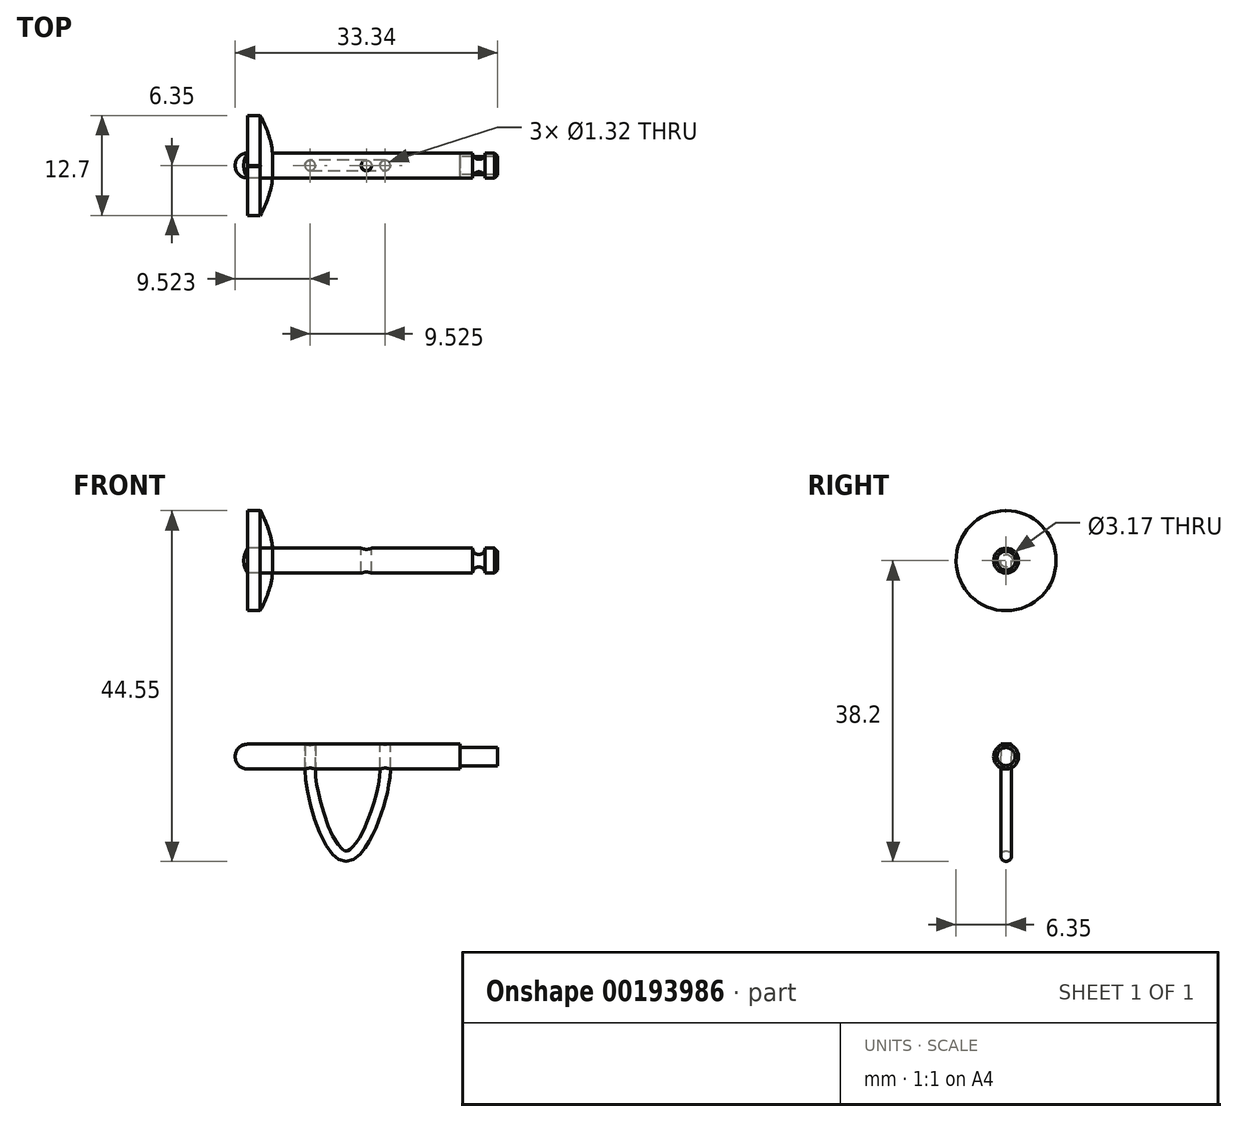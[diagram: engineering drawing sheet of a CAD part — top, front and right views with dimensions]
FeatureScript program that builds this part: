
annotation { "Feature Type Name" : "Feature", "Feature Type Description" : "" }
export const myFeature = defineFeature(function(context is Context, id is Id, definition is map)
    precondition{}
    {
        {
            var Q0;
            Q0=qCreatedBy(makeId("Front.planeOp"),FACE);
            var sketch = newSketch(context, id + "F0", { "sketchPlane" : qUnion([Q0])});
            skLineSegment(sketch, "E0", {"start": v(15.88, 0) * mm, "end": v(-15.88, 0) * mm, "construction": true});
            skLineSegment(sketch, "E1", {"start": v(-17.46, -24.9) * mm, "end": v(15.87, -24.9) * mm, "construction": true});
            skLineSegment(sketch, "E2", {"start": v(-15.88, 0) * mm, "end": v(-15.88, 1.59) * mm});
            skLineSegment(sketch, "E3", {"start": v(-15.88, 1.59) * mm, "end": v(12.7, 1.59) * mm});
            skLineSegment(sketch, "E4", {"start": v(14.29, 1.59) * mm, "end": v(15.87, 1.59) * mm});
            skLineSegment(sketch, "E5", {"start": v(15.87, 0) * mm, "end": v(15.87, 1.59) * mm});
            skLineSegment(sketch, "E6", {"start": v(-17.46, -24.9) * mm, "end": v(-17.46, -23.3) * mm});
            skLineSegment(sketch, "E7", {"start": v(-17.46, -23.3) * mm, "end": v(11.11, -23.3) * mm});
            skLineSegment(sketch, "E8", {"start": v(11.11, -23.3) * mm, "end": v(11.11, -23.75) * mm});
            skLineSegment(sketch, "E9", {"start": v(11.11, -23.75) * mm, "end": v(15.87, -23.75) * mm});
            skLineSegment(sketch, "E10", {"start": v(15.87, -23.75) * mm, "end": v(15.87, -24.9) * mm});
            skArc(sketch, "E11", {"start": v(12.7, 1.59) * mm, "mid": v(13.5, 0.8) * mm, "end": v(14.29, 1.59) * mm});
            skLineSegment(sketch, "E12", {"start": v(12.7, 1.59) * mm, "end": v(14.29, 1.59) * mm, "construction": true});
            skArc(sketch, "E13", {"start": v(-15.88, 1.59) * mm, "mid": v(-16.25, 0.83) * mm, "end": v(-16.38, 0) * mm});
            skLineSegment(sketch, "E14", {"start": v(-15.88, 0) * mm, "end": v(15.88, 0) * mm});
            skLineSegment(sketch, "E15", {"start": v(-17.46, -24.9) * mm, "end": v(15.87, -24.9) * mm});
            skLineSegment(sketch, "E16", {"start": v(-15.88, 0) * mm, "end": v(-16.38, 0) * mm, "construction": true});
            skLineSegment(sketch, "E17", {"start": v(-16.38, 0) * mm, "end": v(-16.38, 1.36) * mm, "construction": true});
            skLineSegment(sketch, "E18", {"start": v(-16.38, 0) * mm, "end": v(-15.88, 0) * mm});
            skLineSegment(sketch, "E19", {"start": v(15.87, 0) * mm, "end": v(15.88, -23.75) * mm, "construction": true});
            skSolve(sketch);
        }
        {
            var Q0;
            Q0=makeQuery(id+"F0.imprint","IMPRINT",FACE,{"disambiguationData":[TD([[makeQuery(id+"F0.imprint","IMPRINT",EDGE,{"derivedFrom":sQuery(id+"F0.wireOp",EDGE,"E2")}),-1.0]])]});
            var Q1;
            Q1=makeQuery(id+"F0.imprint","IMPRINT",FACE,{"disambiguationData":[TD([[makeQuery(id+"F0.imprint","IMPRINT",EDGE,{"derivedFrom":sQuery(id+"F0.wireOp",EDGE,"E2")}),1.0]])]});
            var Q2;
            Q2=sQuery(id+"F0.wireOp",EDGE,"E18");
            revolve(context, id + "F1", {"entities" : qUnion([Q0, Q1]), "axis" : qUnion([Q2]), "revolveType" : RevolveType.FULL});
        }
        {
            var Q0;
            Q0=makeQuery(id+"F1.opRevolve","SWEPT_EDGE",EDGE,{"disambiguationData":[OSD([sQuery(id+"F0.wireOp",EDGE,"E4"),sQuery(id+"F0.wireOp",EDGE,"E5")])]});
            chamfer(context, id + "F2", {"entities" : qUnion([Q0]), "width" : 0.4 * mm, "tangentPropagation" : true});
        }
        {
            var Q0;
            Q0=makeQuery(id+"F0.imprint","IMPRINT",FACE,{"disambiguationData":[TD([[makeQuery(id+"F0.imprint","IMPRINT",EDGE,{"derivedFrom":sQuery(id+"F0.wireOp",EDGE,"E6")}),-1.0]])]});
            var Q1;
            Q1=sQuery(id+"F0.wireOp",EDGE,"E15");
            revolve(context, id + "F3", {"entities" : qUnion([Q0]), "axis" : qUnion([Q1]), "revolveType" : RevolveType.FULL});
        }
        {
            var Q0;
            Q0=makeQuery(id+"F3.opRevolve","SWEPT_EDGE",EDGE,{"disambiguationData":[OSD([sQuery(id+"F0.wireOp",EDGE,"E6"),sQuery(id+"F0.wireOp",EDGE,"E7")])]});
            fillet(context, id + "F4", {"entities" : qUnion([Q0]), "radius" : .5 * 3.17 * mm, "tangentPropagation" : true, "allowEdgeOverflow" : false});
        }
        {
            var Q0;
            Q0=qCreatedBy(makeId("Top.planeOp"),FACE);
            cPlane(context, id + "F5", {"entities" : qUnion([Q0]), "cplaneType" : CPlaneType.OFFSET, "offset" : 1.59 * mm, "width" : 152.4 * mm, "height" : 152.4 * mm});
        }
        {
            var Q0;
            Q0=qCreatedBy(id+"F5.planeOp",FACE);
            var sketch = newSketch(context, id + "F6", { "sketchPlane" : qUnion([Q0])});
            skCircle(sketch, "E20", {"center": v(-0.8, 0) * mm, "radius": 0.66 * mm});
            skLineSegment(sketch, "E21", {"start": v(-12.7, 1.6) * mm, "end": v(-12.7, -1.6) * mm, "construction": true});
            skLineSegment(sketch, "E22", {"start": v(11.11, 1.53) * mm, "end": v(11.11, -1.64) * mm, "construction": true});
            skSolve(sketch);
        }
        {
            var Q0;
            Q0=makeQuery(id+"F6.imprint","IMPRINT",FACE,{"disambiguationData":[TD([[makeQuery(id+"F6.imprint","IMPRINT",EDGE,{"derivedFrom":sQuery(id+"F6.wireOp",EDGE,"E20")}),1.0]])]});
            extrude(context, id + "F7", {"entities" : qUnion([Q0]), "operationType" : NewBodyOperationType.REMOVE, "oppositeDirection" : true, "depth" : 3.17 * mm});
        }
        {
            var Q0;
            Q0=qCreatedBy(makeId("Front.planeOp"),FACE);
            var sketch = newSketch(context, id + "F8", { "sketchPlane" : qUnion([Q0])});
            skLineSegment(sketch, "E23", {"start": v(-15.88, 1.59) * mm, "end": v(-15.88, 6.35) * mm});
            skLineSegment(sketch, "E24", {"start": v(-15.88, 6.35) * mm, "end": v(-14.29, 6.35) * mm});
            skArc(sketch, "E25", {"start": v(-12.6, 0) * mm, "mid": v(-13.03, 3.29) * mm, "end": v(-14.29, 6.35) * mm});
            skLineSegment(sketch, "E26", {"start": v(-14.29, 6.35) * mm, "end": v(-14.29, 0) * mm, "construction": true});
            skLineSegment(sketch, "E27", {"start": v(-12.6, 0) * mm, "end": v(-12.6, 4.81) * mm, "construction": true});
            skPoint(sketch, "E28", {"position": v(-12.7, 1.59) * mm});
            skLineSegment(sketch, "E29", {"start": v(-15.88, 1.59) * mm, "end": v(-12.7, 1.59) * mm});
            skSolve(sketch);
        }
        {
            var Q0;
            Q0=makeQuery(id+"F8.imprint","IMPRINT",FACE,{"disambiguationData":[TD([[makeQuery(id+"F8.imprint","IMPRINT",EDGE,{"derivedFrom":sQuery(id+"F8.wireOp",EDGE,"E23")}),-1.0]])]});
            var Q1;
            Q1=sQuery(id+"F0.wireOp",EDGE,"E14");
            revolve(context, id + "F9", {"entities" : qUnion([Q0]), "axis" : qUnion([Q1]), "revolveType" : RevolveType.FULL});
        }
        {
            var Q0;
            Q0=makeQuery(id+"F9.opRevolve","SWEPT_FACE",FACE,{"disambiguationData":[OSD([sQuery(id+"F8.wireOp",EDGE,"E23")])]});
            var sketch = newSketch(context, id + "F10", { "sketchPlane" : qUnion([Q0])});
            skLineSegment(sketch, "E30", {"start": v(0, 6.35) * mm, "end": v(0.05, 6.29) * mm});
            skLineSegment(sketch, "E31", {"start": v(0.05, 6.29) * mm, "end": v(0.1, 6.35) * mm});
            skSolve(sketch);
        }
        {
            var Q0;
            {var subQ0=sQuery(id+"F10.wireOp",EDGE,"E30");Q0=makeQuery(id+"F10.imprint","IMPRINT",FACE,{"disambiguationData":[TD([[makeQuery(id+"F10.imprint","IMPRINT",EDGE,{"derivedFrom":subQ0}),1.0]])]});}
            var Q1;
            Q1=makeQuery(id+"F9.opRevolve","SWEPT_FACE",FACE,{"disambiguationData":[OSD([sQuery(id+"F8.wireOp",EDGE,"E25")])]});
            extrude(context, id + "F11", {"entities" : qUnion([Q0]), "operationType" : NewBodyOperationType.REMOVE, "endBound" : BoundingType.UP_TO_SURFACE, "oppositeDirection" : true, "endBoundEntityFace" : qUnion([Q1]), "depth" : 25.4 * mm});
        }
        {
            var Q0;
            Q0=sQuery(id+"F0.wireOp",EDGE,"E7");
            cPlane(context, id + "F12", {"entities" : qUnion([Q0]), "cplaneType" : CPlaneType.LINE_ANGLE, "offset" : 25.4 * mm, "angle" : 90 * degree, "width" : 152.4 * mm, "height" : 152.4 * mm});
        }
        {
            var Q0;
            Q0=qCreatedBy(id+"F12.planeOp",FACE);
            var sketch = newSketch(context, id + "F13", { "sketchPlane" : qUnion([Q0])});
            skCircle(sketch, "E32", {"center": v(-7.94, 0) * mm, "radius": 0.66 * mm});
            skCircle(sketch, "E33", {"center": v(1.59, 0) * mm, "radius": 0.66 * mm});
            skLineSegment(sketch, "E34", {"start": v(-17.46, 0) * mm, "end": v(11.11, 0) * mm, "construction": true});
            skSolve(sketch);
        }
        {
            var Q0;
            Q0=makeQuery(id+"F13.imprint","IMPRINT",FACE,{"disambiguationData":[TD([[makeQuery(id+"F13.imprint","IMPRINT",EDGE,{"derivedFrom":sQuery(id+"F13.wireOp",EDGE,"E32")}),1.0]])]});
            var Q1;
            Q1=makeQuery(id+"F13.imprint","IMPRINT",FACE,{"disambiguationData":[TD([[makeQuery(id+"F13.imprint","IMPRINT",EDGE,{"derivedFrom":sQuery(id+"F13.wireOp",EDGE,"E33")}),1.0]])]});
            extrude(context, id + "F14", {"entities" : qUnion([Q0, Q1]), "operationType" : NewBodyOperationType.REMOVE, "oppositeDirection" : true, "depth" : 3.17 * mm});
        }
        {
            var Q0;
            Q0=qCreatedBy(makeId("Front.planeOp"),FACE);
            var sketch = newSketch(context, id + "F15", { "sketchPlane" : qUnion([Q0])});
            skLineSegment(sketch, "E35", {"start": v(-7.94, -23.3) * mm, "end": v(-7.94, -26.55) * mm});
            skLineSegment(sketch, "E36", {"start": v(1.59, -23.3) * mm, "end": v(1.59, -26.58) * mm});
            skFitSpline(sketch, "E37", {"points": [v(-7.94, -26.55) * mm, v(-3.36, -37.54) * mm, v(1.59, -26.58) * mm], "startDerivative": vector(0, -18.51) * mm, "endDerivative": vector(0, 18.23) * mm});
            skSolve(sketch);
        }
        {
            var Q0;
            Q0=makeQuery(id+"F13.imprint","IMPRINT",FACE,{"disambiguationData":[TD([[makeQuery(id+"F13.imprint","IMPRINT",EDGE,{"derivedFrom":sQuery(id+"F13.wireOp",EDGE,"E32")}),1.0]])]});
            var Q1;
            Q1=sQuery(id+"F15.wireOp",EDGE,"E35");
            var Q2;
            Q2=sQuery(id+"F15.wireOp",EDGE,"E37");
            var Q3;
            Q3=sQuery(id+"F15.wireOp",EDGE,"E36");
            sweep(context, id + "F16", {"profiles" : qUnion([Q0]), "path" : qUnion([Q1, Q2, Q3])});
        }
    });
